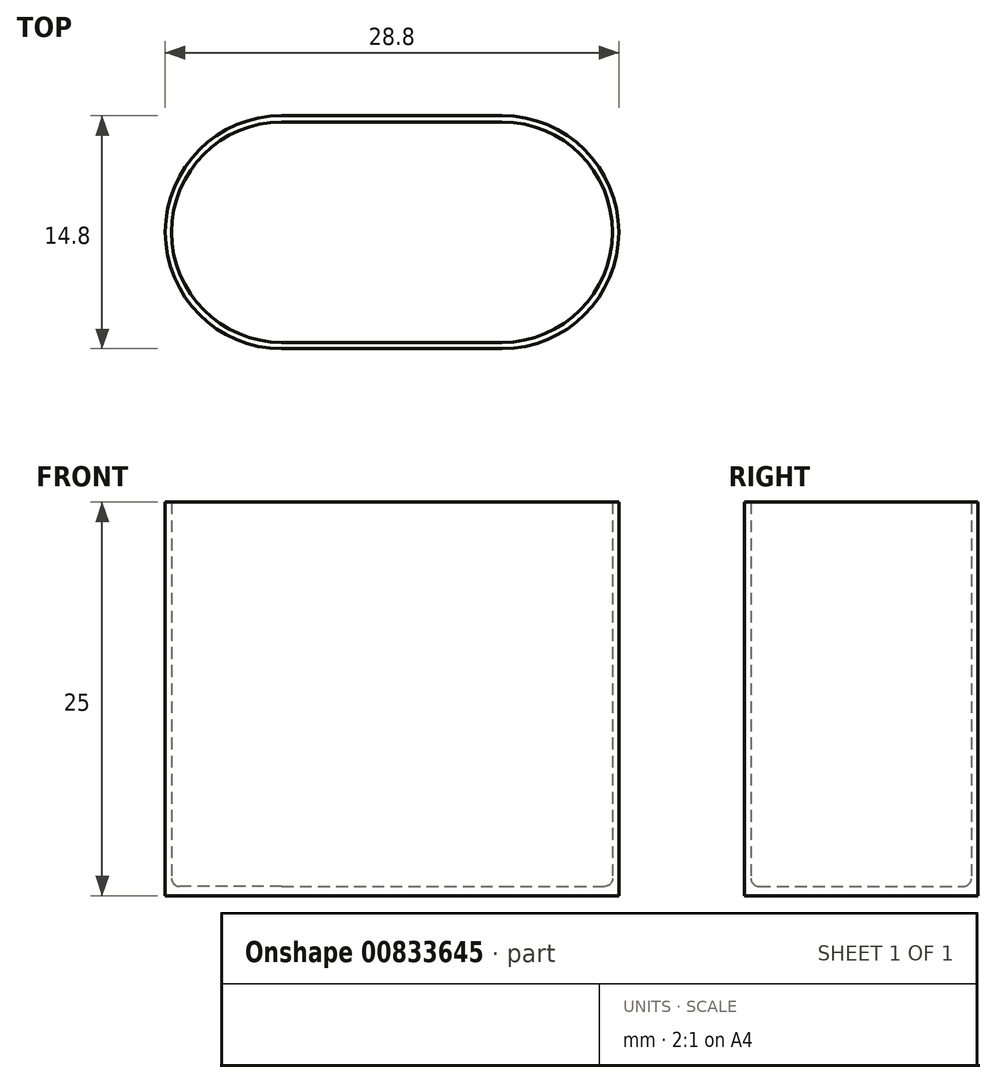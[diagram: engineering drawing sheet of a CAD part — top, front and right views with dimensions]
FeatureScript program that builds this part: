
annotation { "Feature Type Name" : "Feature", "Feature Type Description" : "" }
export const myFeature = defineFeature(function(context is Context, id is Id, definition is map)
    precondition{}
    {
        {
            var Q0;
            Q0=qCreatedBy(makeId("Top.planeOp"),FACE);
            var sketch = newSketch(context, id + "F0", { "sketchPlane" : qUnion([Q0])});
            skCircle(sketch, "E0", {"center": v(0, 0) * mm, "radius": 7 * mm});
            skCircle(sketch, "E1", {"center": v(14, 0) * mm, "radius": 7 * mm});
            skLineSegment(sketch, "E2", {"start": v(0, 7) * mm, "end": v(14, 7) * mm});
            skLineSegment(sketch, "E3", {"start": v(0, -7) * mm, "end": v(14, -7) * mm});
            skCircle(sketch, "E4", {"center": v(0, 0) * mm, "radius": 7.4 * mm});
            skCircle(sketch, "E5", {"center": v(14, 0) * mm, "radius": 7.4 * mm});
            skLineSegment(sketch, "E6", {"start": v(0, 7.4) * mm, "end": v(14, 7.4) * mm});
            skLineSegment(sketch, "E7", {"start": v(0, -7.4) * mm, "end": v(14, -7.4) * mm});
            skSolve(sketch);
        }
        {
            var Q0;
            {var subQ2=sQuery(id+"F0.wireOp",EDGE,"E2");var subQ5=sQuery(id+"F0.wireOp",EDGE,"E0");var subQ8=makeQuery(id+"F0.imprint","INTERSECT",VERTEX,{"derivedFrom":[subQ5,subQ2]});Q0=makeQuery(id+"F0.imprint","IMPRINT",FACE,{"disambiguationData":[TD([[makeQuery(id+"F0.imprint","IMPRINT",EDGE,{"disambiguationData":[TD([[subQ8,-1.0]])],"derivedFrom":subQ5}),-1.0]])]});}
            var Q1;
            {var subQ5=sQuery(id+"F0.wireOp",EDGE,"E6");Q1=makeQuery(id+"F0.imprint","IMPRINT",FACE,{"disambiguationData":[TD([[makeQuery(id+"F0.imprint","IMPRINT",EDGE,{"derivedFrom":subQ5}),-1.0]])]});}
            var Q2;
            {var subQ1=sQuery(id+"F0.wireOp",EDGE,"E1");var subQ5=sQuery(id+"F0.wireOp",EDGE,"E2");var subQ6=makeQuery(id+"F0.imprint","INTERSECT",VERTEX,{"derivedFrom":[subQ1,subQ5]});Q2=makeQuery(id+"F0.imprint","IMPRINT",FACE,{"disambiguationData":[TD([[makeQuery(id+"F0.imprint","IMPRINT",EDGE,{"disambiguationData":[TD([[subQ6,1.0]])],"derivedFrom":subQ1}),-1.0]])]});}
            var Q3;
            {var subQ5=sQuery(id+"F0.wireOp",EDGE,"E7");Q3=makeQuery(id+"F0.imprint","IMPRINT",FACE,{"disambiguationData":[TD([[makeQuery(id+"F0.imprint","IMPRINT",EDGE,{"derivedFrom":subQ5}),1.0]])]});}
            extrude(context, id + "F1", {"entities" : qUnion([Q0, Q1, Q2, Q3]), "depth" : 25 * mm, "offsetDistance" : 25 * mm});
        }
        {
            var Q0;
            {var subQ0=sQuery(id+"F0.wireOp",EDGE,"E0");var subQ1=makeQuery(id+"F0.imprint","INTERSECT",VERTEX,{"derivedFrom":[subQ0,sQuery(id+"F0.wireOp",EDGE,"E2")]});Q0=makeQuery(id+"F0.imprint","IMPRINT",FACE,{"disambiguationData":[TD([[makeQuery(id+"F0.imprint","IMPRINT",EDGE,{"disambiguationData":[TD([[subQ1,1.0]])],"derivedFrom":subQ0}),1.0]])]});}
            var Q1;
            {var subQ0=sQuery(id+"F0.wireOp",EDGE,"E4");var subQ1=sQuery(id+"F0.wireOp",EDGE,"E3");var subQ2=makeQuery(id+"F0.imprint","INTERSECT",VERTEX,{"derivedFrom":[subQ1,subQ0]});Q1=makeQuery(id+"F0.imprint","IMPRINT",FACE,{"disambiguationData":[TD([[makeQuery(id+"F0.imprint","IMPRINT",EDGE,{"disambiguationData":[TD([[subQ2,-1.0]])],"derivedFrom":subQ1}),1.0]])]});}
            var Q2;
            {var subQ0=sQuery(id+"F0.wireOp",EDGE,"E1");var subQ1=makeQuery(id+"F0.imprint","INTERSECT",VERTEX,{"derivedFrom":[subQ0,sQuery(id+"F0.wireOp",EDGE,"E2")]});Q2=makeQuery(id+"F0.imprint","IMPRINT",FACE,{"disambiguationData":[TD([[makeQuery(id+"F0.imprint","IMPRINT",EDGE,{"disambiguationData":[TD([[subQ1,-1.0]])],"derivedFrom":subQ0}),1.0]])]});}
            var Q3;
            {var subQ0=sQuery(id+"F0.wireOp",EDGE,"E3");var subQ1=sQuery(id+"F0.wireOp",EDGE,"E0");var subQ2=makeQuery(id+"F0.imprint","INTERSECT",VERTEX,{"derivedFrom":[subQ1,subQ0]});Q3=makeQuery(id+"F0.imprint","IMPRINT",FACE,{"disambiguationData":[TD([[makeQuery(id+"F0.imprint","IMPRINT",EDGE,{"disambiguationData":[TD([[subQ2,-1.0]])],"derivedFrom":subQ1}),-1.0]])]});}
            var Q4;
            {var subQ0=sQuery(id+"F0.wireOp",EDGE,"E3");var subQ1=sQuery(id+"F0.wireOp",EDGE,"E1");var subQ2=makeQuery(id+"F0.imprint","INTERSECT",VERTEX,{"derivedFrom":[subQ1,subQ0]});Q4=makeQuery(id+"F0.imprint","IMPRINT",FACE,{"disambiguationData":[TD([[makeQuery(id+"F0.imprint","IMPRINT",EDGE,{"disambiguationData":[TD([[subQ2,1.0]])],"derivedFrom":subQ1}),-1.0]])]});}
            var Q5;
            {var subQ0=sQuery(id+"F0.wireOp",EDGE,"E1");var subQ1=sQuery(id+"F0.wireOp",EDGE,"E0");var subQ2=makeQuery(id+"F0.imprint","INTERSECT",VERTEX,{"derivedFrom":[subQ1,subQ0]});Q5=makeQuery(id+"F0.imprint","IMPRINT",FACE,{"disambiguationData":[TD([[makeQuery(id+"F0.imprint","IMPRINT",EDGE,{"disambiguationData":[TD([[subQ2,1.0]])],"derivedFrom":subQ1}),-1.0]])]});}
            var Q6;
            {var subQ0=sQuery(id+"F0.wireOp",EDGE,"E1");var subQ1=makeQuery(id+"F0.imprint","INTERSECT",VERTEX,{"derivedFrom":[sQuery(id+"F0.wireOp",EDGE,"E0"),subQ0]});Q6=makeQuery(id+"F0.imprint","IMPRINT",FACE,{"disambiguationData":[TD([[makeQuery(id+"F0.imprint","IMPRINT",EDGE,{"disambiguationData":[TD([[subQ1,1.0]])],"derivedFrom":subQ0}),1.0]])]});}
            var Q7;
            {var subQ0=sQuery(id+"F0.wireOp",EDGE,"E5");var subQ1=sQuery(id+"F0.wireOp",EDGE,"E0");var subQ2=makeQuery(id+"F0.imprint","INTERSECT",VERTEX,{"disambiguationData":[OD(0.0)],"derivedFrom":[subQ1,subQ0]});Q7=makeQuery(id+"F0.imprint","IMPRINT",FACE,{"disambiguationData":[TD([[makeQuery(id+"F0.imprint","IMPRINT",EDGE,{"disambiguationData":[TD([[subQ2,1.0]])],"derivedFrom":subQ1}),1.0]])]});}
            var Q8;
            {var subQ0=sQuery(id+"F0.wireOp",EDGE,"E2");var subQ1=sQuery(id+"F0.wireOp",EDGE,"E0");var subQ2=makeQuery(id+"F0.imprint","INTERSECT",VERTEX,{"derivedFrom":[subQ1,subQ0]});Q8=makeQuery(id+"F0.imprint","IMPRINT",FACE,{"disambiguationData":[TD([[makeQuery(id+"F0.imprint","IMPRINT",EDGE,{"disambiguationData":[TD([[subQ2,1.0]])],"derivedFrom":subQ1}),-1.0]])]});}
            var Q9;
            {var subQ0=sQuery(id+"F0.wireOp",EDGE,"E2");var subQ1=sQuery(id+"F0.wireOp",EDGE,"E1");var subQ2=makeQuery(id+"F0.imprint","INTERSECT",VERTEX,{"derivedFrom":[subQ1,subQ0]});Q9=makeQuery(id+"F0.imprint","IMPRINT",FACE,{"disambiguationData":[TD([[makeQuery(id+"F0.imprint","IMPRINT",EDGE,{"disambiguationData":[TD([[subQ2,-1.0]])],"derivedFrom":subQ1}),-1.0]])]});}
            var Q10;
            {var subQ0=sQuery(id+"F0.wireOp",EDGE,"E5");var subQ1=sQuery(id+"F0.wireOp",EDGE,"E0");var subQ2=makeQuery(id+"F0.imprint","INTERSECT",VERTEX,{"disambiguationData":[OD(0.0)],"derivedFrom":[subQ1,subQ0]});Q10=makeQuery(id+"F0.imprint","IMPRINT",FACE,{"disambiguationData":[TD([[makeQuery(id+"F0.imprint","IMPRINT",EDGE,{"disambiguationData":[TD([[subQ2,1.0]])],"derivedFrom":subQ1}),-1.0]])]});}
            var Q11;
            {var subQ0=sQuery(id+"F0.wireOp",EDGE,"E4");var subQ1=sQuery(id+"F0.wireOp",EDGE,"E2");var subQ2=makeQuery(id+"F0.imprint","INTERSECT",VERTEX,{"derivedFrom":[subQ1,subQ0]});Q11=makeQuery(id+"F0.imprint","IMPRINT",FACE,{"disambiguationData":[TD([[makeQuery(id+"F0.imprint","IMPRINT",EDGE,{"disambiguationData":[TD([[subQ2,-1.0]])],"derivedFrom":subQ1}),-1.0]])]});}
            extrude(context, id + "F2", {"entities" : qUnion([Q0, Q1, Q2, Q3, Q4, Q5, Q6, Q7, Q8, Q9, Q10, Q11]), "operationType" : NewBodyOperationType.ADD, "depth" : .6 * mm, "offsetDistance" : 25 * mm});
        }
        {
            var Q0;
            Q0=makeQuery(id+"F2.opExtrude","CAP_FACE",FACE,{"disambiguationData":[OSD([sQuery(id+"F0.wireOp",EDGE,"E0"),sQuery(id+"F0.wireOp",EDGE,"E1"),sQuery(id+"F0.wireOp",EDGE,"E2"),sQuery(id+"F0.wireOp",EDGE,"E3")])],"isStart":false});
            fillet(context, id + "F3", {"entities" : qUnion([Q0]), "radius" : .5 * mm, "tangentPropagation" : true, "allowEdgeOverflow" : false});
        }
    });
